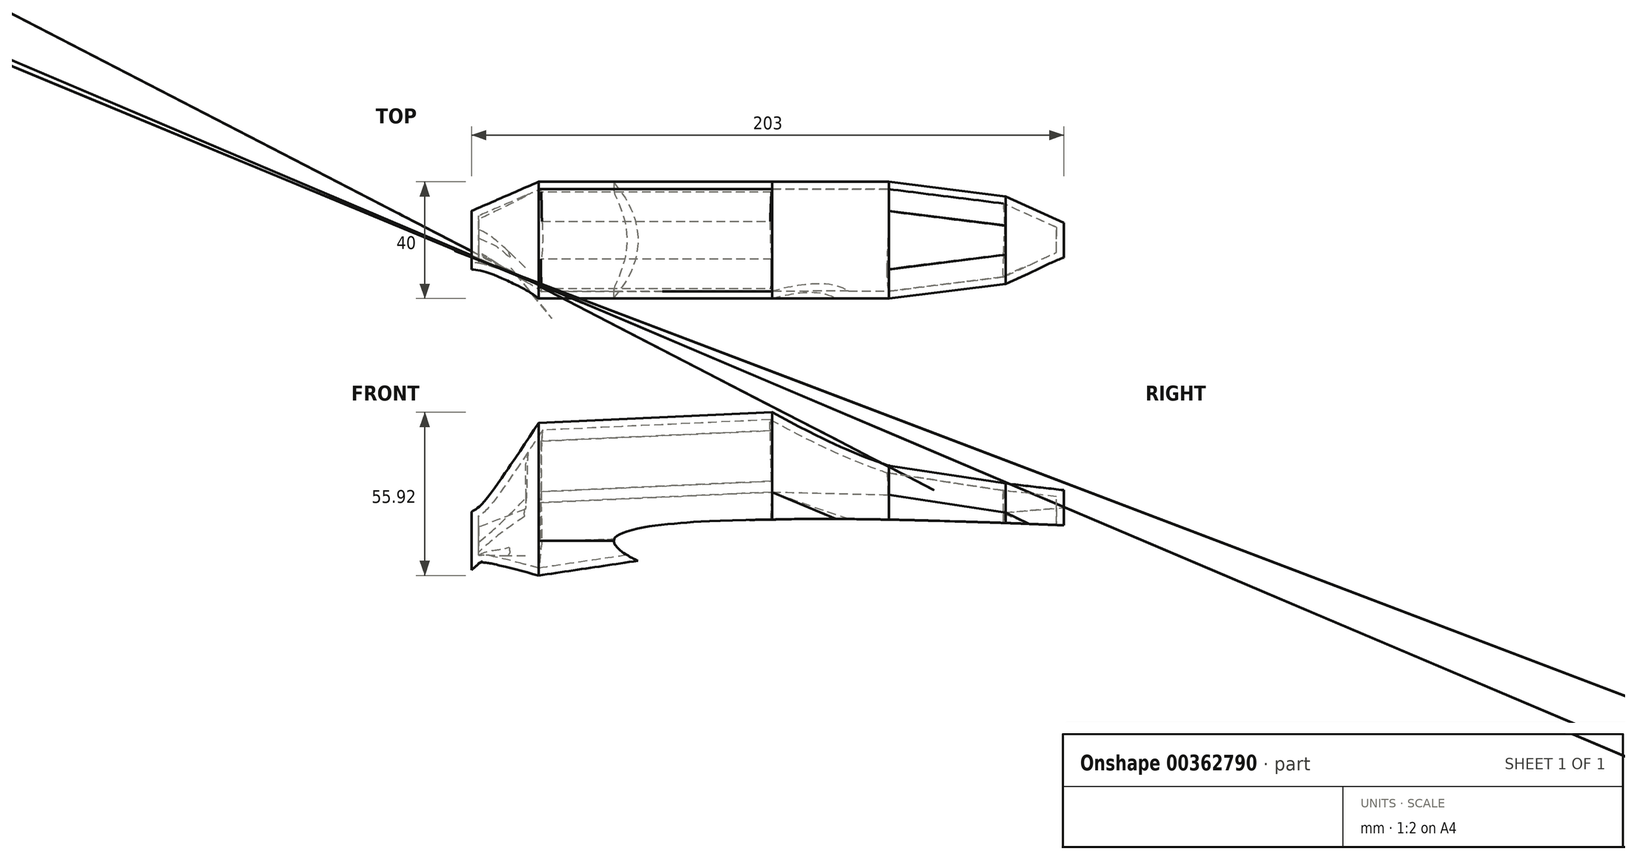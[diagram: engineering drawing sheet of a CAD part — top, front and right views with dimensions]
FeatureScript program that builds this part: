
annotation { "Feature Type Name" : "Feature", "Feature Type Description" : "" }
export const myFeature = defineFeature(function(context is Context, id is Id, definition is map)
    precondition{}
    {
        {
            var Q0;
            Q0=qCreatedBy(makeId("Front.planeOp"),FACE);
            var sketch = newSketch(context, id + "F0", { "sketchPlane" : qUnion([Q0])});
            skLineSegment(sketch, "E0", {"start": v(0, 0) * mm, "end": v(80, 0) * mm});
            skLineSegment(sketch, "E1", {"start": v(80, 0) * mm, "end": v(120, 0) * mm});
            skLineSegment(sketch, "E2", {"start": v(120, 0) * mm, "end": v(160, 0) * mm});
            skLineSegment(sketch, "E3", {"start": v(0, 0) * mm, "end": v(-23, 0) * mm});
            skFitSpline(sketch, "E4.MirrorC", {"points": [v(25.84, 0.14) * mm, v(26.2, -1.34) * mm, v(27.08, -2.35) * mm, v(28.33, -3.55) * mm, v(30.08, -4.7) * mm, v(32.8, -6.23) * mm, v(35.46, -7.4) * mm, v(38.11, -8.38) * mm, v(44.79, -10.16) * mm, v(48.42, -10.93) * mm, v(53, -11.66) * mm, v(60.13, -12.6) * mm, v(65.7, -13.23) * mm, v(74.41, -13.95) * mm, v(88.1, -14.27) * mm, v(105.53, -14.11) * mm, v(121.93, -13.31) * mm, v(140.09, -12.11) * mm, v(156.97, -10.83) * mm, v(169.9, -9.7) * mm, v(184.03, -8.35) * mm, v(203.13, -6.33) * mm, v(218.47, -4.65) * mm, v(234.68, -3.1) * mm, v(252.9, -1.42) * mm, v(264.8, -0.42) * mm, v(275.84, 0.12) * mm, v(266.91, 0.53) * mm, v(261.43, 0.73) * mm, v(246.9, 1.7) * mm, v(235.2, 2.49) * mm, v(226.11, 3) * mm, v(209.6, 3.97) * mm, v(191.03, 4.88) * mm, v(170.07, 5.75) * mm, v(159.92, 6.16) * mm, v(136, 6.9) * mm, v(118.1, 7.34) * mm, v(93.27, 7.6) * mm, v(84.17, 7.42) * mm, v(60.8, 6.9) * mm, v(51, 6.34) * mm, v(44.7, 5.78) * mm, v(38.68, 5.1) * mm, v(33.53, 4.18) * mm, v(29.5, 2.94) * mm, v(27.61, 2.16) * mm, v(26.44, 1.4) * mm, v(25.84, 0.14) * mm]});
            skLineSegment(sketch, "E5", {"start": v(160, 0) * mm, "end": v(180, 0) * mm});
            skSolve(sketch);
        }
        {
            var Q0;
            Q0=sQuery(id+"F0.wireOp",EDGE,"E0");
            var Q1;
            Q1=sQuery(id+"F0.wireOp",VERTEX,"E1.start");
            cPlane(context, id + "F1", {"entities" : qUnion([Q0, Q1]), "cplaneType" : CPlaneType.LINE_POINT, "offset" : 25 * mm, "width" : 150 * mm, "height" : 150 * mm});
        }
        {
            var Q0;
            Q0=sQuery(id+"F0.wireOp",EDGE,"E1");
            var Q1;
            Q1=sQuery(id+"F0.wireOp",VERTEX,"E2.start");
            cPlane(context, id + "F2", {"entities" : qUnion([Q0, Q1]), "cplaneType" : CPlaneType.LINE_POINT, "offset" : 25 * mm, "width" : 150 * mm, "height" : 150 * mm});
        }
        {
            var Q0;
            Q0=sQuery(id+"F0.wireOp",EDGE,"E2");
            var Q1;
            Q1=sQuery(id+"F0.wireOp",VERTEX,"E2.end");
            cPlane(context, id + "F3", {"entities" : qUnion([Q0, Q1]), "cplaneType" : CPlaneType.LINE_POINT, "offset" : 25 * mm, "width" : 150 * mm, "height" : 150 * mm});
        }
        {
            var Q0;
            Q0=sQuery(id+"F0.wireOp",EDGE,"E3");
            var Q1;
            Q1=sQuery(id+"F0.wireOp",VERTEX,"E3.end");
            cPlane(context, id + "F4", {"entities" : qUnion([Q0, Q1]), "cplaneType" : CPlaneType.LINE_POINT, "offset" : 25 * mm, "width" : 150 * mm, "height" : 150 * mm});
        }
        {
            var Q0;
            Q0=qCreatedBy(id+"F4.planeOp",FACE);
            var sketch = newSketch(context, id + "F5", { "sketchPlane" : qUnion([Q0])});
            skCircle(sketch, "E6", {"center": v(0, 0) * mm, "radius": 10 * mm});
            skSolve(sketch);
        }
        {
            var Q0;
            Q0=qCreatedBy(makeId("Right.planeOp"),FACE);
            var sketch = newSketch(context, id + "F6", { "sketchPlane" : qUnion([Q0])});
            skArc(sketch, "E7", {"start": v(20, 13.09) * mm, "mid": v(19.66, 15.68) * mm, "end": v(18.66, 18.09) * mm});
            skArc(sketch, "E8", {"start": v(-18.66, 18.09) * mm, "mid": v(-19.66, 15.68) * mm, "end": v(-20, 13.09) * mm});
            skArc(sketch, "E9", {"start": v(8.66, 35.4) * mm, "mid": v(0, 40.4) * mm, "end": v(-8.66, 35.4) * mm});
            skLineSegment(sketch, "E10", {"start": v(-8.66, 35.4) * mm, "end": v(-18.66, 18.09) * mm});
            skLineSegment(sketch, "E11", {"start": v(18.66, 18.09) * mm, "end": v(8.66, 35.4) * mm});
            skLineSegment(sketch, "E12", {"start": v(-20, 13.09) * mm, "end": v(-20, 0) * mm});
            skLineSegment(sketch, "E13", {"start": v(20, 0) * mm, "end": v(20, 13.09) * mm});
            skEllipticalArc(sketch, "E14", {});
            const initialGuessF6  = {"E14": [0, 0, -1, 0, 0.02, 0.011848411419733682, 0, 3.141592653589793]};
            skSetInitialGuess(sketch, initialGuessF6);
            skSolve(sketch);
        }
        {
            var Q0;
            Q0=qCreatedBy(id+"F1.planeOp",FACE);
            var sketch = newSketch(context, id + "F7", { "sketchPlane" : qUnion([Q0])});
            skArc(sketch, "E15", {"start": v(20, 16.75) * mm, "mid": v(19.66, 19.34) * mm, "end": v(18.66, 21.75) * mm});
            skArc(sketch, "E16", {"start": v(-18.66, 21.75) * mm, "mid": v(-19.66, 19.34) * mm, "end": v(-20, 16.75) * mm});
            skArc(sketch, "E17", {"start": v(8.66, 39.07) * mm, "mid": v(0, 44.07) * mm, "end": v(-8.66, 39.07) * mm});
            skLineSegment(sketch, "E18", {"start": v(-8.66, 39.07) * mm, "end": v(-18.66, 21.75) * mm});
            skLineSegment(sketch, "E19", {"start": v(18.66, 21.75) * mm, "end": v(8.66, 39.07) * mm});
            skLineSegment(sketch, "E20", {"start": v(-20, 16.75) * mm, "end": v(-20, 0) * mm});
            skLineSegment(sketch, "E21", {"start": v(-20, 0) * mm, "end": v(20, 0) * mm});
            skLineSegment(sketch, "E22", {"start": v(20, 0) * mm, "end": v(20, 16.75) * mm});
            skPoint(sketch, "E23", {"position": v(0, 0) * mm});
            skSolve(sketch);
        }
        {
            var Q0;
            Q0=qCreatedBy(id+"F2.planeOp",FACE);
            var sketch = newSketch(context, id + "F8", { "sketchPlane" : qUnion([Q0])});
            skLineSegment(sketch, "E24", {"start": v(-20, 0) * mm, "end": v(-20, 15.82) * mm});
            skLineSegment(sketch, "E25", {"start": v(-10, 25.82) * mm, "end": v(10, 25.82) * mm});
            skLineSegment(sketch, "E26", {"start": v(20, 15.82) * mm, "end": v(20, 0) * mm});
            skPoint(sketch, "E27", {"position": v(0, 0) * mm});
            skArc(sketch, "E28", {"start": v(20, 15.82) * mm, "mid": v(17.07, 22.89) * mm, "end": v(10, 25.82) * mm});
            skArc(sketch, "E29", {"start": v(-10, 25.82) * mm, "mid": v(-17.07, 22.89) * mm, "end": v(-20, 15.82) * mm});
            skPoint(sketch, "E30.orphan", {"position": v(20, 25.82) * mm});
            skPoint(sketch, "E31.orphan", {"position": v(-20, 25.82) * mm});
            skLineSegment(sketch, "E32", {"start": v(20, 0) * mm, "end": v(-20, 0) * mm});
            skSolve(sketch);
        }
        {
            var Q0;
            Q0=qCreatedBy(id+"F3.planeOp",FACE);
            var sketch = newSketch(context, id + "F9", { "sketchPlane" : qUnion([Q0])});
            skLineSegment(sketch, "E33", {"start": v(15, 0) * mm, "end": v(-15, 0) * mm});
            skLineSegment(sketch, "E34", {"start": v(-15, 0) * mm, "end": v(-15, 9.7) * mm});
            skLineSegment(sketch, "E35", {"start": v(-5, 19.7) * mm, "end": v(5, 19.7) * mm});
            skLineSegment(sketch, "E36", {"start": v(15, 9.7) * mm, "end": v(15, 0) * mm});
            skPoint(sketch, "E37", {"position": v(0, 0) * mm});
            skArc(sketch, "E38", {"start": v(15, 9.7) * mm, "mid": v(12.07, 16.76) * mm, "end": v(5, 19.7) * mm});
            skArc(sketch, "E39", {"start": v(-5, 19.7) * mm, "mid": v(-12.07, 16.76) * mm, "end": v(-15, 9.7) * mm});
            skSolve(sketch);
        }
        {
            var Q0;
            Q0=sQuery(id+"F0.wireOp",EDGE,"E5");
            var Q1;
            Q1=sQuery(id+"F0.wireOp",VERTEX,"E5.end");
            cPlane(context, id + "F10", {"entities" : qUnion([Q0, Q1]), "cplaneType" : CPlaneType.LINE_POINT, "offset" : 25 * mm, "width" : 150 * mm, "height" : 150 * mm});
        }
        {
            var Q0;
            Q0=qCreatedBy(id+"F10.planeOp",FACE);
            var sketch = newSketch(context, id + "F11", { "sketchPlane" : qUnion([Q0])});
            skArc(sketch, "E40", {"start": v(6, 11.41) * mm, "mid": v(0, 17.41) * mm, "end": v(-6, 11.41) * mm});
            skLineSegment(sketch, "E41", {"start": v(0, 0) * mm, "end": v(6, 0) * mm});
            skLineSegment(sketch, "E42", {"start": v(6, 0) * mm, "end": v(6, 11.41) * mm});
            skLineSegment(sketch, "E43", {"start": v(0, 0) * mm, "end": v(-6, 0) * mm});
            skLineSegment(sketch, "E44", {"start": v(-6, 0) * mm, "end": v(-6, 11.41) * mm});
            skSolve(sketch);
        }
        {
            var Q0;
            Q0=makeQuery(id+"F6.imprint","IMPRINT",FACE,{"disambiguationData":[TD([[makeQuery(id+"F6.imprint","IMPRINT",EDGE,{"derivedFrom":sQuery(id+"F6.wireOp",EDGE,"E7")}),1.0]])]});
            var Q1;
            Q1=makeQuery(id+"F7.imprint","IMPRINT",FACE,{"disambiguationData":[TD([[makeQuery(id+"F7.imprint","IMPRINT",EDGE,{"derivedFrom":sQuery(id+"F7.wireOp",EDGE,"E15")}),1.0]])]});
            loft(context, id + "F12", {"sheetProfilesArray" : [{ "sheetProfileEntities" : qUnion([Q0]) }, { "sheetProfileEntities" : qUnion([Q1]) }]});
        }
        {
            var Q1;
            Q1=makeQuery(id+"F12.opLoft","CAP_FACE",FACE,{"disambiguationData":[OSD([makeQuery(id+"F6.imprint","IMPRINT",FACE,{"disambiguationData":[TD([[makeQuery(id+"F6.imprint","IMPRINT",EDGE,{"derivedFrom":sQuery(id+"F6.wireOp",EDGE,"E7")}),1.0]])]})])],"isStart":true});
            var Q2;
            Q2=makeQuery(id+"F5.imprint","IMPRINT",FACE,{"disambiguationData":[TD([[makeQuery(id+"F5.imprint","IMPRINT",EDGE,{"derivedFrom":sQuery(id+"F5.wireOp",EDGE,"E6")}),1.0]])]});
            loft(context, id + "F13", {"operationType" : NewBodyOperationType.ADD, "sheetProfilesArray" : [{ "sheetProfileEntities" : qUnion([Q1]) }, { "sheetProfileEntities" : qUnion([Q2]) }]});
        }
        {
            var Q1;
            Q1=makeQuery(id+"F12.opLoft","CAP_FACE",FACE,{"disambiguationData":[OSD([makeQuery(id+"F7.imprint","IMPRINT",FACE,{"disambiguationData":[TD([[makeQuery(id+"F7.imprint","IMPRINT",EDGE,{"derivedFrom":sQuery(id+"F7.wireOp",EDGE,"E15")}),1.0]])]})])],"isStart":true});
            var Q2;
            Q2=makeQuery(id+"F8.imprint","IMPRINT",FACE,{"disambiguationData":[TD([[makeQuery(id+"F8.imprint","IMPRINT",EDGE,{"derivedFrom":sQuery(id+"F8.wireOp",EDGE,"E24")}),-1.0]])]});
            loft(context, id + "F14", {"operationType" : NewBodyOperationType.ADD, "sheetProfilesArray" : [{ "sheetProfileEntities" : qUnion([Q1]) }, { "sheetProfileEntities" : qUnion([Q2]) }]});
        }
        {
            var Q1;
            Q1=makeQuery(id+"F14.opLoft","CAP_FACE",FACE,{"disambiguationData":[OSD([makeQuery(id+"F8.imprint","IMPRINT",FACE,{"disambiguationData":[TD([[makeQuery(id+"F8.imprint","IMPRINT",EDGE,{"derivedFrom":sQuery(id+"F8.wireOp",EDGE,"E24")}),-1.0]])]})])],"isStart":true});
            var Q2;
            Q2=makeQuery(id+"F9.imprint","IMPRINT",FACE,{"disambiguationData":[TD([[makeQuery(id+"F9.imprint","IMPRINT",EDGE,{"derivedFrom":sQuery(id+"F9.wireOp",EDGE,"E33")}),-1.0]])]});
            loft(context, id + "F15", {"operationType" : NewBodyOperationType.ADD, "sheetProfilesArray" : [{ "sheetProfileEntities" : qUnion([Q1]) }, { "sheetProfileEntities" : qUnion([Q2]) }]});
        }
        {
            var Q1;
            Q1=makeQuery(id+"F15.opLoft","CAP_FACE",FACE,{"disambiguationData":[OSD([makeQuery(id+"F9.imprint","IMPRINT",FACE,{"disambiguationData":[TD([[makeQuery(id+"F9.imprint","IMPRINT",EDGE,{"derivedFrom":sQuery(id+"F9.wireOp",EDGE,"E33")}),-1.0]])]})])],"isStart":true});
            var Q2;
            Q2=makeQuery(id+"F11.imprint","IMPRINT",FACE,{"disambiguationData":[TD([[makeQuery(id+"F11.imprint","IMPRINT",EDGE,{"derivedFrom":sQuery(id+"F11.wireOp",EDGE,"E40")}),1.0]])]});
            loft(context, id + "F16", {"operationType" : NewBodyOperationType.ADD, "sheetProfilesArray" : [{ "sheetProfileEntities" : qUnion([Q1]) }, { "sheetProfileEntities" : qUnion([Q2]) }]});
        }
        {
            var Q0;
            Q0=makeQuery(id+"F0.imprint","IMPRINT",FACE,{"disambiguationData":[TD([[makeQuery(id+"F0.imprint","IMPRINT",EDGE,{"derivedFrom":sQuery(id+"F0.wireOp",EDGE,"E4.MirrorC")}),1.0]])]});
            extrude(context, id + "F17", {"entities" : qUnion([Q0]), "operationType" : NewBodyOperationType.REMOVE, "depth" : 100 * mm, "hasSecondDirection" : true, "secondDirectionOppositeDirection" : true, "secondDirectionDepth" : 100 * mm});
        }
        {
            var Q0;
            Q0=makeQuery(id+"F17.boolean.opBoolean","COPY",FACE,{"derivedFrom":makeQuery(id+"F17.opExtrude","SWEPT_FACE",FACE,{"disambiguationData":[OSD([sQuery(id+"F0.wireOp",EDGE,"E4.MirrorC")])]})});
            shell(context, id + "F18", {"entities" : qUnion([Q0]), "thickness" : 2.5 * mm});
        }
    });
